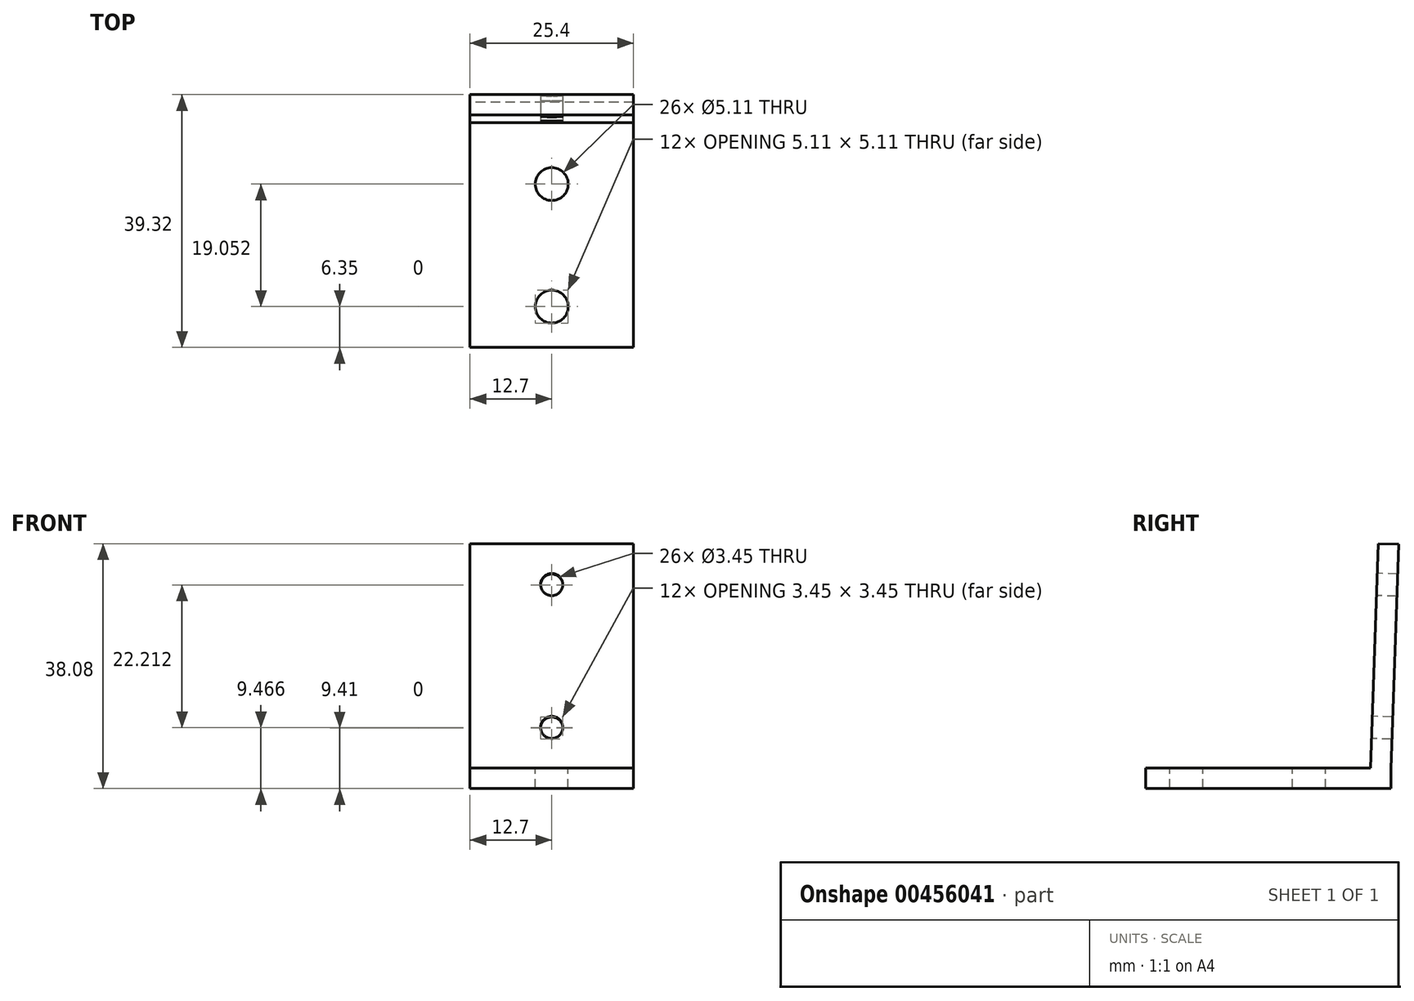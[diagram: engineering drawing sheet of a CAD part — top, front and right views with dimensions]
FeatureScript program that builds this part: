
annotation { "Feature Type Name" : "Feature", "Feature Type Description" : "" }
export const myFeature = defineFeature(function(context is Context, id is Id, definition is map)
    precondition{}
    {
        {
            var Q0;
            Q0=qCreatedBy(makeId("Right.planeOp"),FACE);
            var sketch = newSketch(context, id + "F0", { "sketchPlane" : qUnion([Q0])});
            skLineSegment(sketch, "E0", {"start": v(0, 0) * mm, "end": v(-38.1, 0) * mm});
            skLineSegment(sketch, "E1", {"start": v(-38.1, 0) * mm, "end": v(-38.1, 3.18) * mm});
            skLineSegment(sketch, "E2", {"start": v(-38.1, 3.18) * mm, "end": v(-3.17, 3.18) * mm});
            skLineSegment(sketch, "E3", {"start": v(-3.17, 3.18) * mm, "end": v(-1.95, 38.08) * mm});
            skLineSegment(sketch, "E4", {"start": v(-1.95, 38.08) * mm, "end": v(1.22, 37.97) * mm});
            skLineSegment(sketch, "E5", {"start": v(1.22, 37.97) * mm, "end": v(0, 3.06) * mm});
            skLineSegment(sketch, "E6", {"start": v(0, 3.06) * mm, "end": v(0, 0) * mm});
            skLineSegment(sketch, "E7", {"start": v(-3.17, 3.18) * mm, "end": v(0, 3.06) * mm, "construction": true});
            skSolve(sketch);
        }
        {
            var Q0;
            Q0=makeQuery(id+"F0.imprint","IMPRINT",FACE,{"disambiguationData":[TD([[makeQuery(id+"F0.imprint","IMPRINT",EDGE,{"derivedFrom":sQuery(id+"F0.wireOp",EDGE,"E0")}),-1.0]])]});
            extrude(context, id + "F1", {"entities" : qUnion([Q0]), "depth" : 25.4 * mm});
        }
        {
            var Q0;
            Q0=makeQuery(id+"F1.opExtrude","SWEPT_FACE",FACE,{"disambiguationData":[OSD([sQuery(id+"F0.wireOp",EDGE,"E2")])]});
            var sketch = newSketch(context, id + "F2", { "sketchPlane" : qUnion([Q0])});
            skLineSegment(sketch, "E8", {"start": v(12.7, -38.1) * mm, "end": v(12.7, -3.17) * mm, "construction": true});
            skPoint(sketch, "E9", {"position": v(12.7, -31.75) * mm});
            skPoint(sketch, "E10", {"position": v(12.7, -12.7) * mm});
            skSolve(sketch);
        }
        {
            var Q0;
            Q0=sQuery(id+"F2.wireOp",VERTEX,"E9");
            var Q1;
            Q1=sQuery(id+"F2.wireOp",VERTEX,"E10");
            var Q2;
            Q2=makeQuery(id+"F1.opExtrude","SWEPT_BODY",BODY,{"disambiguationData":[OSD([sQuery(id+"F0.wireOp",EDGE,"E0"),sQuery(id+"F0.wireOp",EDGE,"E1"),sQuery(id+"F0.wireOp",EDGE,"E2"),sQuery(id+"F0.wireOp",EDGE,"E3"),sQuery(id+"F0.wireOp",EDGE,"E4"),sQuery(id+"F0.wireOp",EDGE,"E5"),sQuery(id+"F0.wireOp",EDGE,"E6")])]});
            hole(context, id + "F3", {"style" : HoleStyle.SIMPLE, "endStyle" : HoleEndStyle.THROUGH, "standardTappedOrClearance" : lookupTablePath({ "standard" : "ANSI", "fit" : "Normal (ASME)", "size" : "#10", "type" : "Clearance" }), "standardBlindInLast" : lookupTablePath({ "fit" : "Free", "standard" : "ANSI", "size" : "#10", "type" : "Clearance" }), "holeDiameter" : 5.1 * mm, "isTappedThrough" : true, "tappedDepth" : 8.9 * mm, "tapClearance" : 3, "locations" : qUnion([Q0, Q1]), "scope" : qUnion([Q2])});
        }
        {
            var Q0;
            Q0=makeQuery(id+"F1.opExtrude","SWEPT_FACE",FACE,{"disambiguationData":[OSD([sQuery(id+"F0.wireOp",EDGE,"E3")])]});
            var sketch = newSketch(context, id + "F4", { "sketchPlane" : qUnion([Q0])});
            skLineSegment(sketch, "E11", {"start": v(12.7, 3.06) * mm, "end": v(12.7, 37.99) * mm, "construction": true});
            skPoint(sketch, "E12", {"position": v(12.7, 9.41) * mm});
            skPoint(sketch, "E13", {"position": v(12.7, 31.64) * mm});
            skSolve(sketch);
        }
        {
            var Q0;
            Q0=sQuery(id+"F4.wireOp",VERTEX,"E12");
            var Q1;
            Q1=sQuery(id+"F4.wireOp",VERTEX,"E13");
            var Q2;
            Q2=makeQuery(id+"F1.opExtrude","SWEPT_BODY",BODY,{"disambiguationData":[OSD([sQuery(id+"F0.wireOp",EDGE,"E0"),sQuery(id+"F0.wireOp",EDGE,"E1"),sQuery(id+"F0.wireOp",EDGE,"E2"),sQuery(id+"F0.wireOp",EDGE,"E3"),sQuery(id+"F0.wireOp",EDGE,"E4"),sQuery(id+"F0.wireOp",EDGE,"E5"),sQuery(id+"F0.wireOp",EDGE,"E6")])]});
            hole(context, id + "F5", {"style" : HoleStyle.SIMPLE, "endStyle" : HoleEndStyle.THROUGH, "standardTappedOrClearance" : lookupTablePath({ "standard" : "ANSI", "engagement" : "75%", "pitch" : "32 tpi", "size" : "#8", "type" : "Tapped" }), "standardBlindInLast" : lookupTablePath({ "standard" : "ANSI", "engagement" : "75%", "pitch" : "32 tpi", "size" : "#8", "type" : "Tapped" }), "holeDiameter" : 3.45 * mm, "showTappedDepth" : true, "isTappedThrough" : true, "tappedDepth" : 8.9 * mm, "tapClearance" : 3, "locations" : qUnion([Q0, Q1]), "scope" : qUnion([Q2]), "majorDiameter" : 4.17 * mm});
        }
    });
